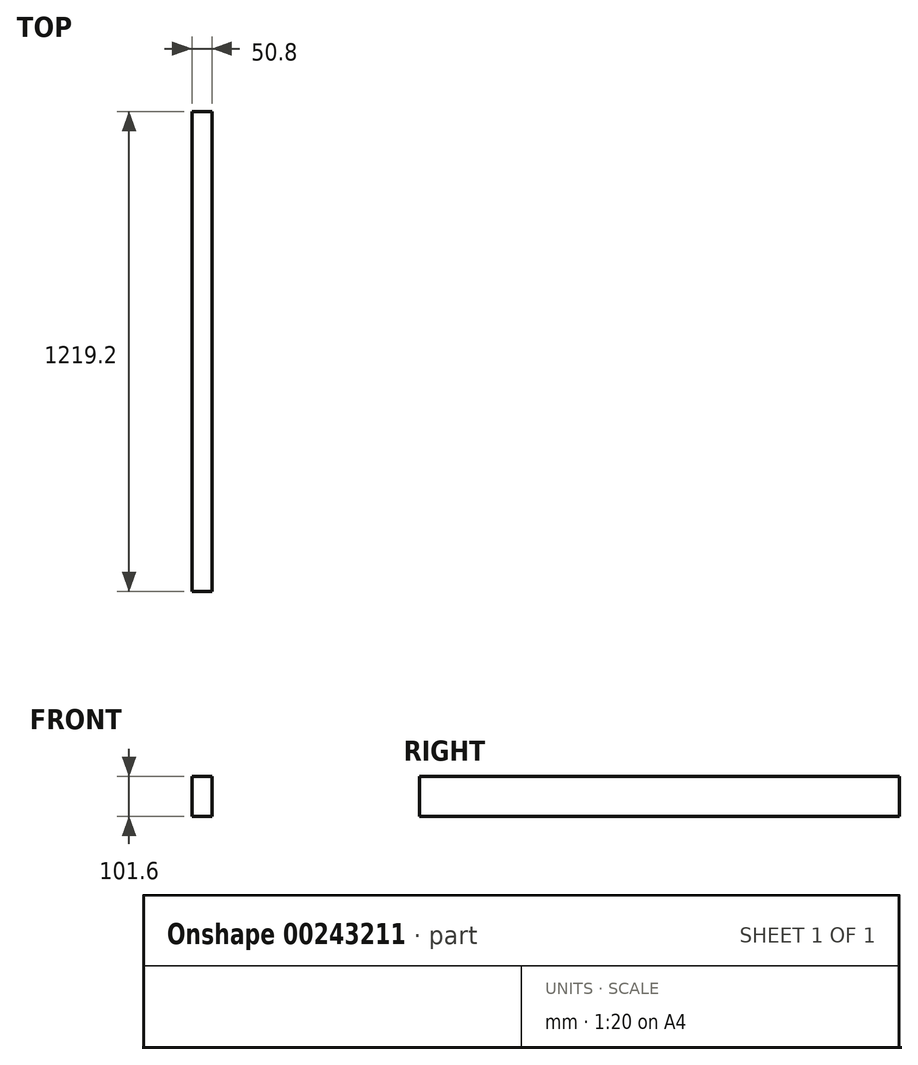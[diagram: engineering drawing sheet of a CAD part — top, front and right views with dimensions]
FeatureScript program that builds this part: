
annotation { "Feature Type Name" : "Feature", "Feature Type Description" : "" }
export const myFeature = defineFeature(function(context is Context, id is Id, definition is map)
    precondition{}
    {
        {
            var Q0;
            Q0=qCreatedBy(makeId("Front.planeOp"),FACE);
            var sketch = newSketch(context, id + "F0", { "sketchPlane" : qUnion([Q0])});
            skLineSegment(sketch, "E0.bottom", {"start": v(25.4, -50.8) * mm, "end": v(-25.4, -50.8) * mm});
            skLineSegment(sketch, "E0.top", {"start": v(25.4, 50.8) * mm, "end": v(-25.4, 50.8) * mm});
            skLineSegment(sketch, "E0.left", {"start": v(25.4, -50.8) * mm, "end": v(25.4, 50.8) * mm});
            skLineSegment(sketch, "E0.right", {"start": v(-25.4, -50.8) * mm, "end": v(-25.4, 50.8) * mm});
            skPoint(sketch, "E0.middle", {"position": v(0, 0) * mm});
            skSolve(sketch);
        }
        {
            var Q0;
            Q0 = qSketchRegion(id + "F0", true);
            extrude(context, id + "F1", {"entities" : qUnion([Q0]), "depth" : 1219.2 * mm});
        }
    });
